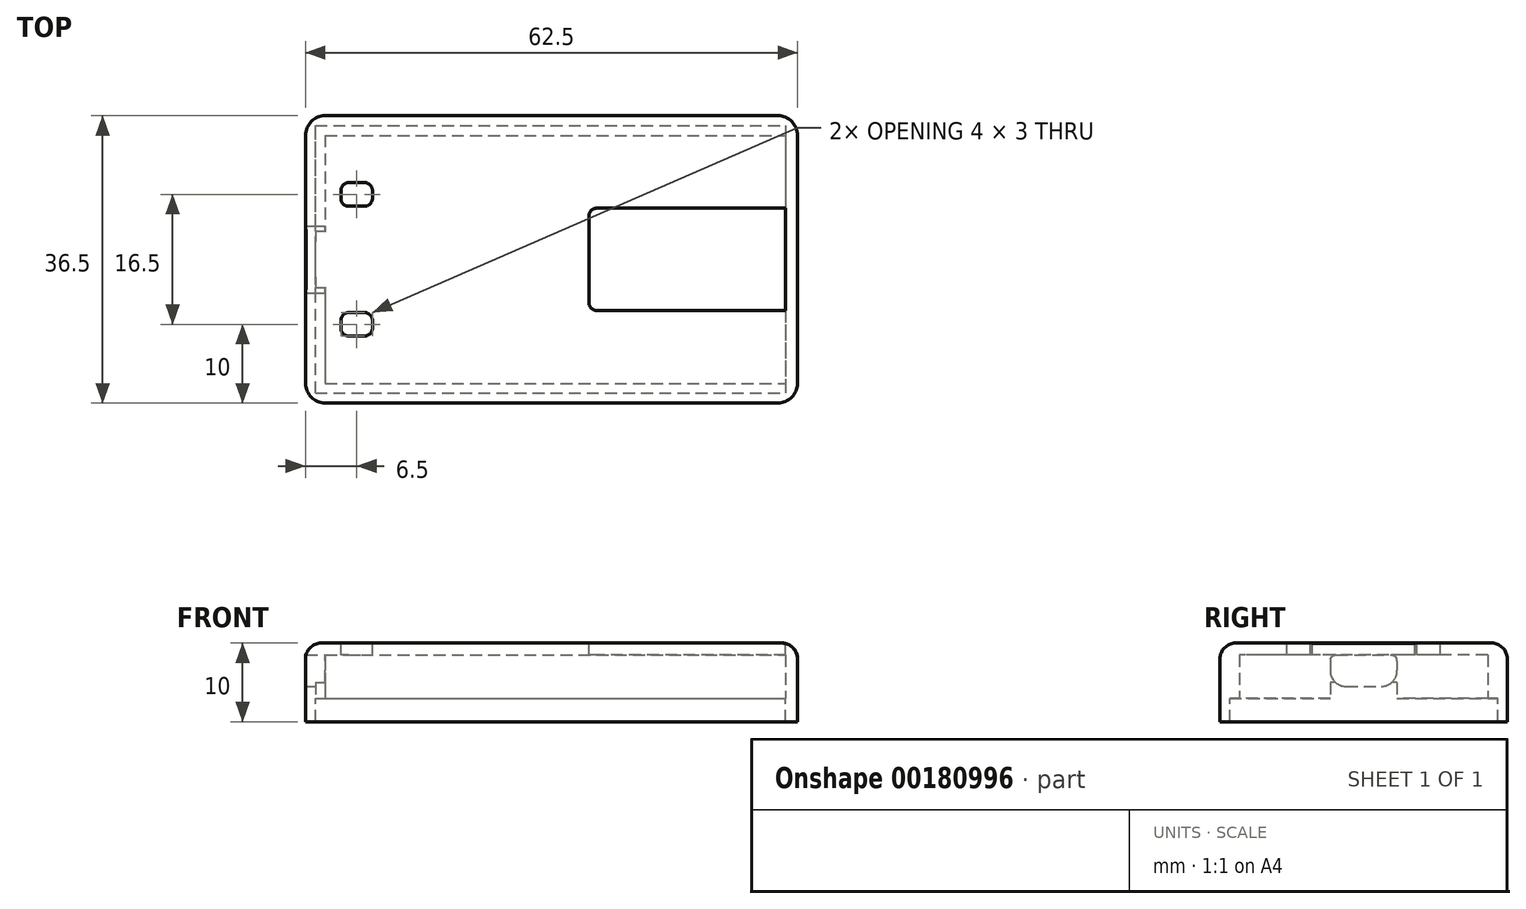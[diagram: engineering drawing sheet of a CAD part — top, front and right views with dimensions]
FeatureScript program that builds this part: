
annotation { "Feature Type Name" : "Feature", "Feature Type Description" : "" }
export const myFeature = defineFeature(function(context is Context, id is Id, definition is map)
    precondition{}
    {
        {
            var Q0;
            Q0=qCreatedBy(makeId("Top.planeOp"),FACE);
            var sketch = newSketch(context, id + "F0", { "sketchPlane" : qUnion([Q0])});
            skLineSegment(sketch, "E0.bottom", {"start": v(-30.75, 18.75) * mm, "end": v(31.75, 18.75) * mm});
            skLineSegment(sketch, "E0.top", {"start": v(-30.75, -17.75) * mm, "end": v(31.75, -17.75) * mm});
            skLineSegment(sketch, "E0.left", {"start": v(-30.75, 18.75) * mm, "end": v(-30.75, -17.75) * mm});
            skLineSegment(sketch, "E0.right", {"start": v(31.75, 18.75) * mm, "end": v(31.75, -17.75) * mm});
            skLineSegment(sketch, "E1.bottom", {"start": v(-28.25, 16.25) * mm, "end": v(30.25, 16.25) * mm});
            skLineSegment(sketch, "E1.top", {"start": v(-28.25, -15.25) * mm, "end": v(30.25, -15.25) * mm});
            skLineSegment(sketch, "E1.left", {"start": v(-28.25, 16.25) * mm, "end": v(-28.25, -15.25) * mm});
            skLineSegment(sketch, "E1.right", {"start": v(30.25, 16.25) * mm, "end": v(30.25, -15.25) * mm});
            skSolve(sketch);
        }
        {
            var Q0;
            Q0=makeQuery(id+"F0.imprint","IMPRINT",FACE,{"disambiguationData":[TD([[makeQuery(id+"F0.imprint","IMPRINT",EDGE,{"derivedFrom":sQuery(id+"F0.wireOp",EDGE,"E0.bottom")}),-1.0]])]});
            extrude(context, id + "F1", {"entities" : qUnion([Q0]), "depth" : 7 * mm});
        }
        {
            var Q0;
            Q0=makeQuery(id+"F1.opExtrude","CAP_FACE",FACE,{"disambiguationData":[OSD([sQuery(id+"F0.wireOp",EDGE,"E0.bottom"),sQuery(id+"F0.wireOp",EDGE,"E0.top"),sQuery(id+"F0.wireOp",EDGE,"E0.left"),sQuery(id+"F0.wireOp",EDGE,"E0.right"),sQuery(id+"F0.wireOp",EDGE,"E1.bottom"),sQuery(id+"F0.wireOp",EDGE,"E1.top"),sQuery(id+"F0.wireOp",EDGE,"E1.left"),sQuery(id+"F0.wireOp",EDGE,"E1.right")])],"isStart":false});
            var sketch = newSketch(context, id + "F2", { "sketchPlane" : qUnion([Q0])});
            skLineSegment(sketch, "E2.bottom", {"start": v(-28.25, 16.25) * mm, "end": v(30.25, 16.25) * mm});
            skLineSegment(sketch, "E2.top", {"start": v(-28.25, -15.25) * mm, "end": v(30.25, -15.25) * mm});
            skLineSegment(sketch, "E2.left", {"start": v(-28.25, 16.25) * mm, "end": v(-28.25, -15.25) * mm});
            skLineSegment(sketch, "E3.bottom", {"start": v(30.25, 7) * mm, "end": v(5.25, 7) * mm});
            skLineSegment(sketch, "E3.top", {"start": v(30.25, -6) * mm, "end": v(5.25, -6) * mm});
            skLineSegment(sketch, "E3.right", {"start": v(5.25, 7) * mm, "end": v(5.25, -6) * mm});
            skLineSegment(sketch, "E4.bottom", {"start": v(-26.25, 10.25) * mm, "end": v(-22.25, 10.25) * mm});
            skLineSegment(sketch, "E4.top", {"start": v(-26.25, 7.25) * mm, "end": v(-22.25, 7.25) * mm});
            skLineSegment(sketch, "E4.left", {"start": v(-26.25, 10.25) * mm, "end": v(-26.25, 7.25) * mm});
            skLineSegment(sketch, "E4.right", {"start": v(-22.25, 10.25) * mm, "end": v(-22.25, 7.25) * mm});
            skLineSegment(sketch, "E5.bottom", {"start": v(-26.25, -6.25) * mm, "end": v(-22.25, -6.25) * mm});
            skLineSegment(sketch, "E5.top", {"start": v(-26.25, -9.25) * mm, "end": v(-22.25, -9.25) * mm});
            skLineSegment(sketch, "E5.left", {"start": v(-26.25, -6.25) * mm, "end": v(-26.25, -9.25) * mm});
            skLineSegment(sketch, "E5.right", {"start": v(-22.25, -6.25) * mm, "end": v(-22.25, -9.25) * mm});
            skLineSegment(sketch, "E6", {"start": v(30.25, 16.25) * mm, "end": v(30.25, 7) * mm});
            skLineSegment(sketch, "E7", {"start": v(30.25, -6) * mm, "end": v(30.25, -15.25) * mm});
            skSolve(sketch);
        }
        {
            var Q0;
            Q0=makeQuery(id+"F2.imprint","IMPRINT",FACE,{"disambiguationData":[TD([[makeQuery(id+"F2.imprint","IMPRINT",EDGE,{"derivedFrom":sQuery(id+"F2.wireOp",EDGE,"E2.bottom")}),-1.0]])]});
            extrude(context, id + "F3", {"entities" : qUnion([Q0]), "operationType" : NewBodyOperationType.ADD, "oppositeDirection" : true, "depth" : 1.5 * mm});
        }
        {
            var Q0;
            Q0=makeQuery(id+"F1.opExtrude","CAP_FACE",FACE,{"disambiguationData":[OSD([sQuery(id+"F0.wireOp",EDGE,"E0.bottom"),sQuery(id+"F0.wireOp",EDGE,"E0.top"),sQuery(id+"F0.wireOp",EDGE,"E0.left"),sQuery(id+"F0.wireOp",EDGE,"E0.right"),sQuery(id+"F0.wireOp",EDGE,"E1.bottom"),sQuery(id+"F0.wireOp",EDGE,"E1.top"),sQuery(id+"F0.wireOp",EDGE,"E1.left"),sQuery(id+"F0.wireOp",EDGE,"E1.right")])],"isStart":true});
            var sketch = newSketch(context, id + "F4", { "sketchPlane" : qUnion([Q0])});
            skLineSegment(sketch, "E8.bottom", {"start": v(-30.75, 17.75) * mm, "end": v(31.75, 17.75) * mm});
            skLineSegment(sketch, "E8.top", {"start": v(-30.75, -18.75) * mm, "end": v(31.75, -18.75) * mm});
            skLineSegment(sketch, "E8.left", {"start": v(-30.75, 17.75) * mm, "end": v(-30.75, -18.75) * mm});
            skLineSegment(sketch, "E8.right", {"start": v(31.75, 17.75) * mm, "end": v(31.75, -18.75) * mm});
            skLineSegment(sketch, "E9.bottom", {"start": v(-29.5, 16.5) * mm, "end": v(30.25, 16.5) * mm});
            skLineSegment(sketch, "E9.top", {"start": v(-29.5, -17.52) * mm, "end": v(30.25, -17.52) * mm});
            skLineSegment(sketch, "E9.left", {"start": v(-29.5, 16.5) * mm, "end": v(-29.5, -17.52) * mm});
            skLineSegment(sketch, "E9.right", {"start": v(30.25, 16.5) * mm, "end": v(30.25, -17.52) * mm});
            skSolve(sketch);
        }
        {
            var Q0;
            Q0=makeQuery(id+"F4.imprint","IMPRINT",FACE,{"disambiguationData":[TD([[makeQuery(id+"F4.imprint","IMPRINT",EDGE,{"derivedFrom":sQuery(id+"F4.wireOp",EDGE,"E8.bottom")}),-1.0]])]});
            var Q1;
            {var subQ5=makeQuery(id+"F1.opExtrude","CAP_EDGE",EDGE,{"disambiguationData":[OSD([sQuery(id+"F0.wireOp",EDGE,"E1.right")])],"isStart":true});Q1=makeQuery(id+"F4.imprint","IMPRINT",FACE,{"disambiguationData":[TD([[makeQuery(id+"F4.imprint","IMPRINT",EDGE,{"derivedFrom":subQ5}),1.0]])]});}
            extrude(context, id + "F5", {"entities" : qUnion([Q0, Q1]), "operationType" : NewBodyOperationType.ADD, "depth" : 3 * mm});
        }
        {
            var Q0;
            Q0=makeQuery(id+"F1.opExtrude","SWEPT_FACE",FACE,{"disambiguationData":[OSD([sQuery(id+"F0.wireOp",EDGE,"E1.left")])]});
            var sketch = newSketch(context, id + "F6", { "sketchPlane" : qUnion([Q0])});
            skLineSegment(sketch, "E10.bottom", {"start": v(-3, 5.5) * mm, "end": v(4, 5.5) * mm});
            skLineSegment(sketch, "E10.top", {"start": v(-1.75, 1.5) * mm, "end": v(2.75, 1.5) * mm});
            skLineSegment(sketch, "E10.left", {"start": v(-3.75, 4.75) * mm, "end": v(-3.75, 3.5) * mm});
            skLineSegment(sketch, "E10.right", {"start": v(4.75, 4.75) * mm, "end": v(4.75, 3.5) * mm});
            skPoint(sketch, "E11.visualSharp", {"position": v(-3.75, 1.5) * mm});
            skArc(sketch, "E11.filletArc", {"start": v(-3.75, 3.5) * mm, "mid": v(-3.16, 2.09) * mm, "end": v(-1.75, 1.5) * mm});
            skPoint(sketch, "E12.visualSharp", {"position": v(4.75, 1.5) * mm});
            skArc(sketch, "E12.filletArc", {"start": v(2.75, 1.5) * mm, "mid": v(4.16, 2.09) * mm, "end": v(4.75, 3.5) * mm});
            skPoint(sketch, "E13.visualSharp", {"position": v(4.75, 5.5) * mm});
            skArc(sketch, "E13.filletArc", {"start": v(4.75, 4.75) * mm, "mid": v(4.53, 5.28) * mm, "end": v(4, 5.5) * mm});
            skPoint(sketch, "E14.visualSharp", {"position": v(-3.75, 5.5) * mm});
            skArc(sketch, "E14.filletArc", {"start": v(-3, 5.5) * mm, "mid": v(-3.53, 5.28) * mm, "end": v(-3.75, 4.75) * mm});
            skSolve(sketch);
        }
        {
            var Q0;
            Q0=makeQuery(id+"F6.imprint","IMPRINT",FACE,{"disambiguationData":[TD([[makeQuery(id+"F6.imprint","IMPRINT",EDGE,{"derivedFrom":sQuery(id+"F6.wireOp",EDGE,"E10.bottom")}),1.0]])]});
            extrude(context, id + "F7", {"entities" : qUnion([Q0]), "operationType" : NewBodyOperationType.REMOVE, "oppositeDirection" : true, "depth" : 2.5 * mm});
        }
        {
            var Q0;
            Q0=makeQuery(id+"F5.boolean.opBoolean","MERGE",EDGE,{"derivedFrom":[makeQuery(id+"F1.opExtrude","SWEPT_EDGE",EDGE,{"disambiguationData":[OSD([sQuery(id+"F0.wireOp",EDGE,"E0.bottom"),sQuery(id+"F0.wireOp",EDGE,"E0.left")])]}),makeQuery(id+"F5.opExtrude","SWEPT_EDGE",EDGE,{"disambiguationData":[OSD([sQuery(id+"F4.wireOp",EDGE,"E8.top"),sQuery(id+"F4.wireOp",EDGE,"E8.left")])]})]});
            var Q1;
            Q1=makeQuery(id+"F5.boolean.opBoolean","MERGE",EDGE,{"derivedFrom":[makeQuery(id+"F1.opExtrude","SWEPT_EDGE",EDGE,{"disambiguationData":[OSD([sQuery(id+"F0.wireOp",EDGE,"E0.top"),sQuery(id+"F0.wireOp",EDGE,"E0.left")])]}),makeQuery(id+"F5.opExtrude","SWEPT_EDGE",EDGE,{"disambiguationData":[OSD([sQuery(id+"F4.wireOp",EDGE,"E8.bottom"),sQuery(id+"F4.wireOp",EDGE,"E8.left")])]})]});
            var Q2;
            Q2=makeQuery(id+"F5.boolean.opBoolean","MERGE",EDGE,{"derivedFrom":[makeQuery(id+"F1.opExtrude","SWEPT_EDGE",EDGE,{"disambiguationData":[OSD([sQuery(id+"F0.wireOp",EDGE,"E0.bottom"),sQuery(id+"F0.wireOp",EDGE,"E0.right")])]}),makeQuery(id+"F5.opExtrude","SWEPT_EDGE",EDGE,{"disambiguationData":[OSD([sQuery(id+"F4.wireOp",EDGE,"E8.top"),sQuery(id+"F4.wireOp",EDGE,"E8.right")])]})]});
            var Q3;
            Q3=makeQuery(id+"F5.boolean.opBoolean","MERGE",EDGE,{"derivedFrom":[makeQuery(id+"F1.opExtrude","SWEPT_EDGE",EDGE,{"disambiguationData":[OSD([sQuery(id+"F0.wireOp",EDGE,"E0.top"),sQuery(id+"F0.wireOp",EDGE,"E0.right")])]}),makeQuery(id+"F5.opExtrude","SWEPT_EDGE",EDGE,{"disambiguationData":[OSD([sQuery(id+"F4.wireOp",EDGE,"E8.bottom"),sQuery(id+"F4.wireOp",EDGE,"E8.right")])]})]});
            fillet(context, id + "F8", {"entities" : qUnion([Q0, Q1, Q2, Q3]), "radius" : 2.5 * mm, "tangentPropagation" : true, "allowEdgeOverflow" : false});
        }
        {
            var Q0;
            Q0=makeQuery(id+"F3.opExtrude","SWEPT_EDGE",EDGE,{"disambiguationData":[OSD([sQuery(id+"F2.wireOp",EDGE,"E3.bottom"),sQuery(id+"F2.wireOp",EDGE,"E3.right")])]});
            var Q1;
            Q1=makeQuery(id+"F3.opExtrude","SWEPT_EDGE",EDGE,{"disambiguationData":[OSD([sQuery(id+"F0.wireOp",EDGE,"E1.right"),sQuery(id+"F2.wireOp",EDGE,"E3.bottom"),sQuery(id+"F2.wireOp",EDGE,"E6")])]});
            var Q2;
            Q2=makeQuery(id+"F3.opExtrude","SWEPT_EDGE",EDGE,{"disambiguationData":[OSD([sQuery(id+"F0.wireOp",EDGE,"E1.right"),sQuery(id+"F2.wireOp",EDGE,"E3.top"),sQuery(id+"F2.wireOp",EDGE,"E7")])]});
            var Q3;
            Q3=makeQuery(id+"F3.opExtrude","SWEPT_EDGE",EDGE,{"disambiguationData":[OSD([sQuery(id+"F2.wireOp",EDGE,"E3.top"),sQuery(id+"F2.wireOp",EDGE,"E3.right")])]});
            fillet(context, id + "F9", {"entities" : qUnion([Q0, Q1, Q2, Q3]), "radius" : 1 * mm, "tangentPropagation" : true, "allowEdgeOverflow" : false});
        }
        {
            var Q0;
            Q0=makeQuery(id+"F3.opExtrude","SWEPT_EDGE",EDGE,{"disambiguationData":[OSD([sQuery(id+"F2.wireOp",EDGE,"E4.bottom"),sQuery(id+"F2.wireOp",EDGE,"E4.right")])]});
            var Q1;
            Q1=makeQuery(id+"F3.opExtrude","SWEPT_EDGE",EDGE,{"disambiguationData":[OSD([sQuery(id+"F2.wireOp",EDGE,"E4.bottom"),sQuery(id+"F2.wireOp",EDGE,"E4.left")])]});
            var Q2;
            Q2=makeQuery(id+"F3.opExtrude","SWEPT_EDGE",EDGE,{"disambiguationData":[OSD([sQuery(id+"F2.wireOp",EDGE,"E4.top"),sQuery(id+"F2.wireOp",EDGE,"E4.left")])]});
            var Q3;
            Q3=makeQuery(id+"F3.opExtrude","SWEPT_EDGE",EDGE,{"disambiguationData":[OSD([sQuery(id+"F2.wireOp",EDGE,"E4.top"),sQuery(id+"F2.wireOp",EDGE,"E4.right")])]});
            var Q4;
            Q4=makeQuery(id+"F3.opExtrude","SWEPT_EDGE",EDGE,{"disambiguationData":[OSD([sQuery(id+"F2.wireOp",EDGE,"E5.bottom"),sQuery(id+"F2.wireOp",EDGE,"E5.left")])]});
            var Q5;
            Q5=makeQuery(id+"F3.opExtrude","SWEPT_EDGE",EDGE,{"disambiguationData":[OSD([sQuery(id+"F2.wireOp",EDGE,"E5.bottom"),sQuery(id+"F2.wireOp",EDGE,"E5.right")])]});
            var Q6;
            Q6=makeQuery(id+"F3.opExtrude","SWEPT_EDGE",EDGE,{"disambiguationData":[OSD([sQuery(id+"F2.wireOp",EDGE,"E5.top"),sQuery(id+"F2.wireOp",EDGE,"E5.right")])]});
            var Q7;
            Q7=makeQuery(id+"F3.opExtrude","SWEPT_EDGE",EDGE,{"disambiguationData":[OSD([sQuery(id+"F2.wireOp",EDGE,"E5.top"),sQuery(id+"F2.wireOp",EDGE,"E5.left")])]});
            fillet(context, id + "F10", {"entities" : qUnion([Q0, Q1, Q2, Q3, Q4, Q5, Q6, Q7]), "radius" : 1 * mm, "tangentPropagation" : true, "allowEdgeOverflow" : false});
        }
        {
            var Q0;
            Q0=makeQuery(id+"F1.opExtrude","CAP_EDGE",EDGE,{"disambiguationData":[OSD([sQuery(id+"F0.wireOp",EDGE,"E0.top")])],"isStart":false});
            fillet(context, id + "F11", {"entities" : qUnion([Q0]), "radius" : 2 * mm, "tangentPropagation" : true, "allowEdgeOverflow" : false});
        }
        {
            var Q0;
            Q0=makeQuery(id+"F1.opExtrude","CAP_FACE",FACE,{"disambiguationData":[OSD([sQuery(id+"F0.wireOp",EDGE,"E0.bottom"),sQuery(id+"F0.wireOp",EDGE,"E0.top"),sQuery(id+"F0.wireOp",EDGE,"E0.left"),sQuery(id+"F0.wireOp",EDGE,"E0.right"),sQuery(id+"F0.wireOp",EDGE,"E1.bottom"),sQuery(id+"F0.wireOp",EDGE,"E1.top"),sQuery(id+"F0.wireOp",EDGE,"E1.left"),sQuery(id+"F0.wireOp",EDGE,"E1.right")])],"isStart":true});
            var sketch = newSketch(context, id + "F12", { "sketchPlane" : qUnion([Q0])});
            skLineSegment(sketch, "E15.bottom", {"start": v(-29.5, 3.75) * mm, "end": v(-28.25, 3.75) * mm});
            skLineSegment(sketch, "E15.top", {"start": v(-29.5, -4.75) * mm, "end": v(-28.25, -4.75) * mm});
            skLineSegment(sketch, "E15.left", {"start": v(-29.5, 3.75) * mm, "end": v(-29.5, -4.75) * mm});
            skLineSegment(sketch, "E15.right", {"start": v(-28.25, 3.75) * mm, "end": v(-28.25, -4.75) * mm});
            skSolve(sketch);
        }
        {
            var Q0;
            Q0=makeQuery(id+"F12.imprint","IMPRINT",FACE,{"disambiguationData":[TD([[makeQuery(id+"F12.imprint","IMPRINT",EDGE,{"derivedFrom":sQuery(id+"F12.wireOp",EDGE,"E15.bottom")}),-1.0]])]});
            extrude(context, id + "F13", {"entities" : qUnion([Q0]), "operationType" : NewBodyOperationType.REMOVE, "oppositeDirection" : true, "depth" : 2 * mm});
        }
    });
